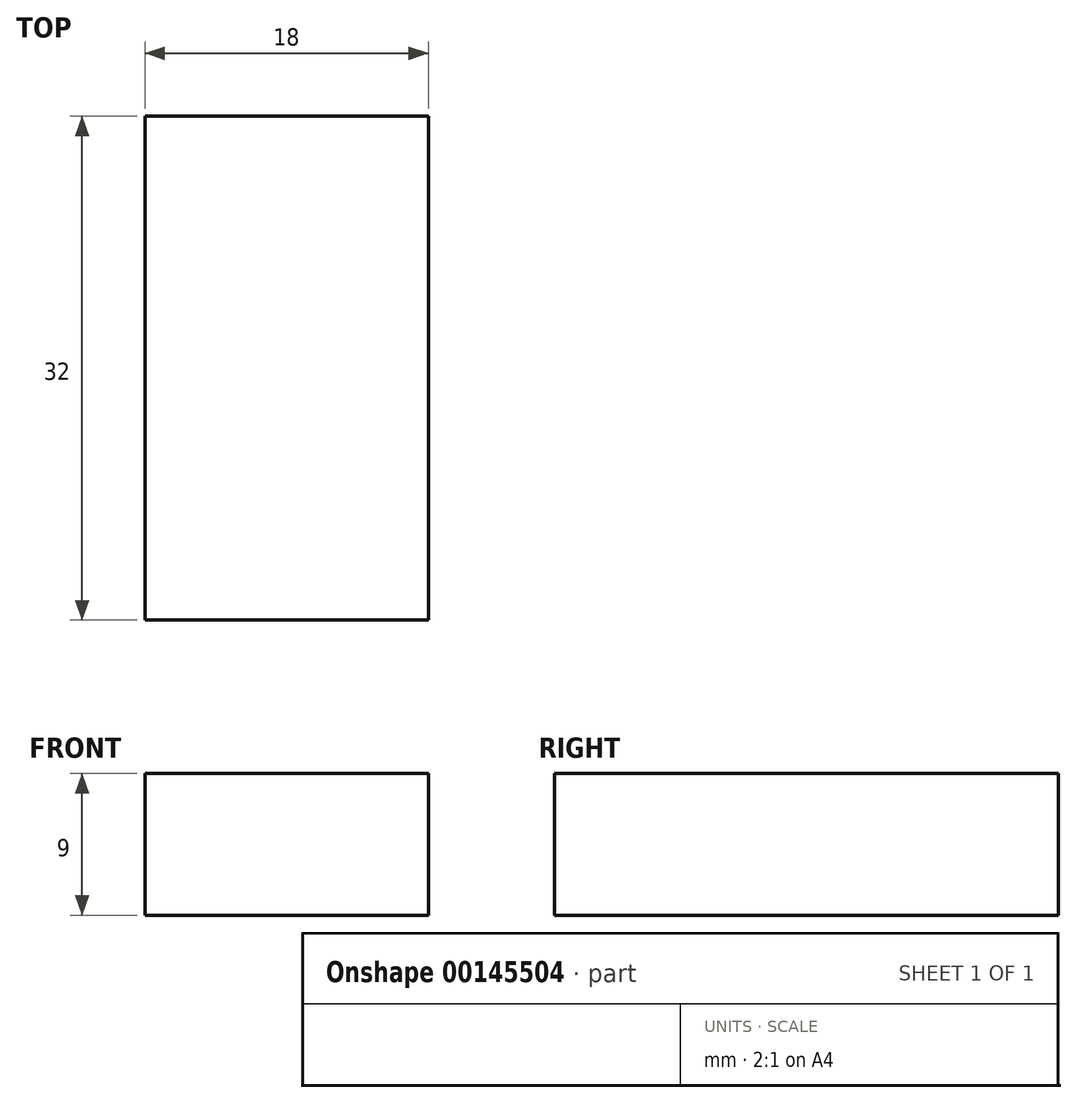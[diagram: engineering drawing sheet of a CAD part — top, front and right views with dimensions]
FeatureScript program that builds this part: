
annotation { "Feature Type Name" : "Feature", "Feature Type Description" : "" }
export const myFeature = defineFeature(function(context is Context, id is Id, definition is map)
    precondition{}
    {
        {
            var Q0;
            Q0=qCreatedBy(makeId("Front.planeOp"),FACE);
            var sketch = newSketch(context, id + "F0", { "sketchPlane" : qUnion([Q0])});
            skLineSegment(sketch, "E0.bottom", {"start": v(9, 6.63) * mm, "end": v(-9, 6.63) * mm});
            skLineSegment(sketch, "E0.top", {"start": v(9, 15.63) * mm, "end": v(-9, 15.63) * mm});
            skLineSegment(sketch, "E0.left", {"start": v(9, 6.63) * mm, "end": v(9, 15.63) * mm});
            skLineSegment(sketch, "E0.right", {"start": v(-9, 6.63) * mm, "end": v(-9, 15.63) * mm});
            skPoint(sketch, "E0.middle", {"position": v(0, 11.13) * mm});
            skSolve(sketch);
        }
        {
            var Q0;
            Q0 = qSketchRegion(id + "F0", true);
            var Q1;
            Q1=makeQuery(id+"F0.imprint","IMPRINT",FACE,{"disambiguationData":[TD([[makeQuery(id+"F0.imprint","IMPRINT",EDGE,{"derivedFrom":sQuery(id+"F0.wireOp",EDGE,"E0.bottom")}),-1.0]])]});
            extrude(context, id + "F1", {"entities" : qUnion([Q0, Q1]), "depth" : 32 * mm});
        }
    });
